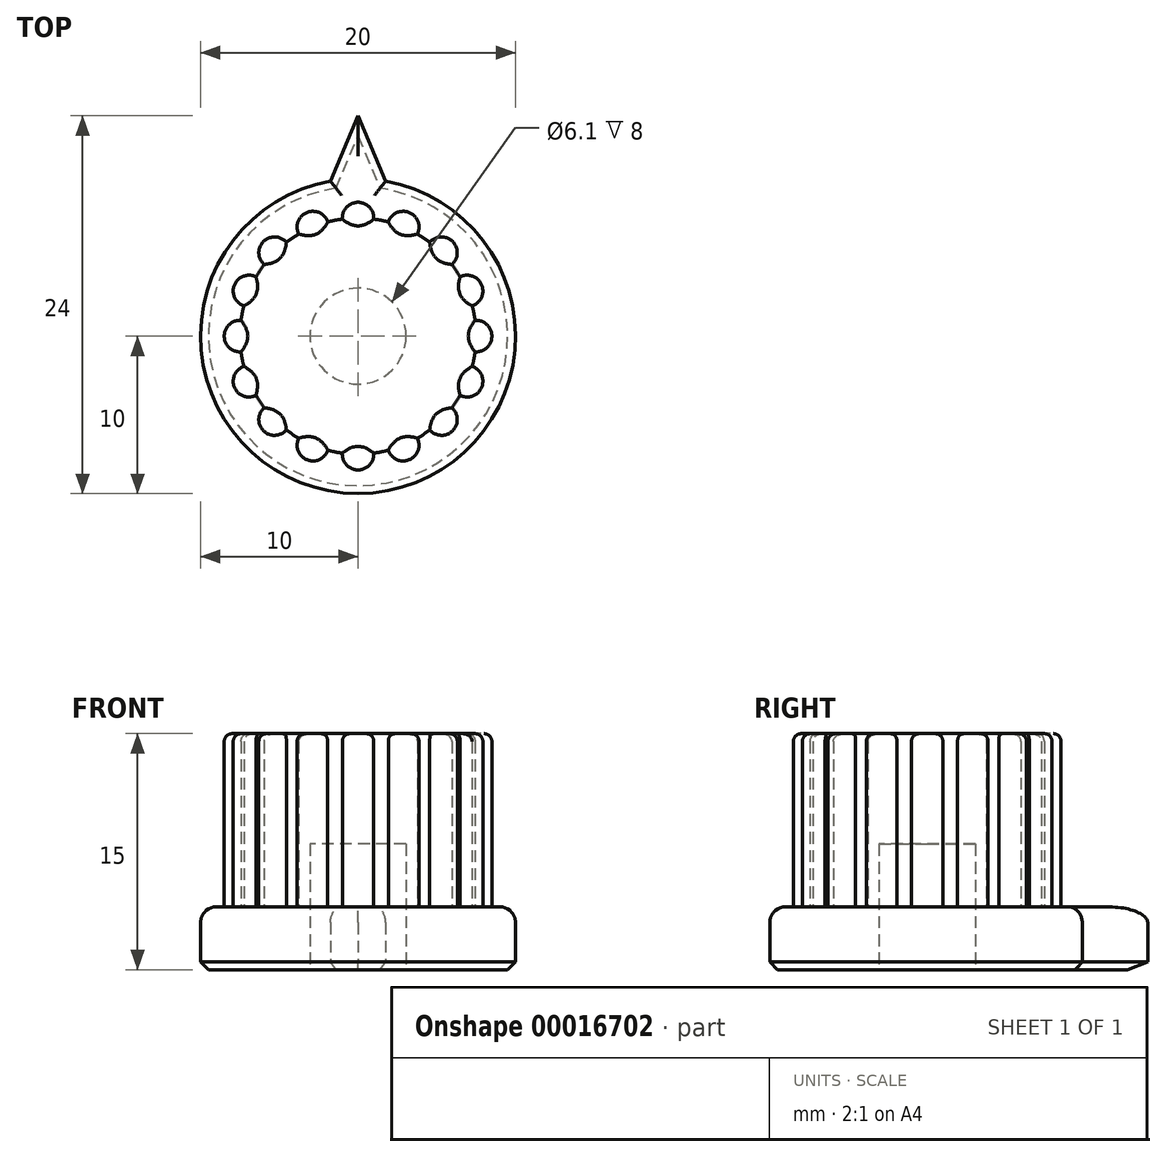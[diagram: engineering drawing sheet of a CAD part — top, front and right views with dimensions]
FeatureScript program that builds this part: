
annotation { "Feature Type Name" : "Feature", "Feature Type Description" : "" }
export const myFeature = defineFeature(function(context is Context, id is Id, definition is map)
    precondition{}
    {
        {
            var Q0;
            Q0=qCreatedBy(makeId("Top.planeOp"),FACE);
            var sketch = newSketch(context, id + "F0", { "sketchPlane" : qUnion([Q0])});
            skCircle(sketch, "E0", {"center": v(0, 0) * mm, "radius": 7.5 * mm});
            skCircle(sketch, "E1", {"center": v(0, 0) * mm, "radius": 10 * mm});
            skCircle(sketch, "E2", {"center": v(0, 0) * mm, "radius": 3.05 * mm});
            skCircle(sketch, "E3", {"center": v(0, 7.5) * mm, "radius": 1 * mm});
            skCircle(sketch, "E4.1.0", {"center": v(2.87, 6.93) * mm, "radius": 1 * mm});
            skCircle(sketch, "E4.2.0", {"center": v(5.3, 5.3) * mm, "radius": 1 * mm});
            skCircle(sketch, "E4.3.0", {"center": v(6.93, 2.87) * mm, "radius": 1 * mm});
            skCircle(sketch, "E4.4.0", {"center": v(7.5, 0) * mm, "radius": 1 * mm});
            skCircle(sketch, "E4.5.0", {"center": v(6.93, -2.87) * mm, "radius": 1 * mm});
            skCircle(sketch, "E4.6.0", {"center": v(5.3, -5.3) * mm, "radius": 1 * mm});
            skCircle(sketch, "E4.7.0", {"center": v(2.87, -6.93) * mm, "radius": 1 * mm});
            skCircle(sketch, "E4.8.0", {"center": v(0, -7.5) * mm, "radius": 1 * mm});
            skCircle(sketch, "E4.9.0", {"center": v(-2.87, -6.93) * mm, "radius": 1 * mm});
            skCircle(sketch, "E4.10.0", {"center": v(-5.3, -5.3) * mm, "radius": 1 * mm});
            skCircle(sketch, "E4.11.0", {"center": v(-6.93, -2.87) * mm, "radius": 1 * mm});
            skCircle(sketch, "E4.12.0", {"center": v(-7.5, 0) * mm, "radius": 1 * mm});
            skCircle(sketch, "E4.13.0", {"center": v(-6.93, 2.87) * mm, "radius": 1 * mm});
            skCircle(sketch, "E4.14.0", {"center": v(-5.3, 5.3) * mm, "radius": 1 * mm});
            skCircle(sketch, "E4.15.0", {"center": v(-2.87, 6.93) * mm, "radius": 1 * mm});
            skLineSegment(sketch, "E4.anchor1", {"start": v(0, 0) * mm, "end": v(0, 7.5) * mm, "construction": true});
            skLineSegment(sketch, "E4.anchor2", {"start": v(0, 0) * mm, "end": v(-2.87, 6.93) * mm, "construction": true});
            skLineSegment(sketch, "E5", {"start": v(0, 10) * mm, "end": v(0, 14) * mm});
            skLineSegment(sketch, "E6", {"start": v(-1.75, 9.85) * mm, "end": v(0, 14) * mm});
            skLineSegment(sketch, "E7.MirrorCS", {"start": v(1.75, 9.85) * mm, "end": v(0, 14) * mm});
            skSolve(sketch);
        }
        {
            var Q0;
            Q0=makeQuery(id+"F0.imprint","IMPRINT",FACE,{"disambiguationData":[TD([[makeQuery(id+"F0.imprint","IMPRINT",EDGE,{"derivedFrom":sQuery(id+"F0.wireOp",EDGE,"E2")}),-1.0]])]});
            var Q1;
            {var subQ0=sQuery(id+"F0.wireOp",EDGE,"E4.12.0");var subQ1=sQuery(id+"F0.wireOp",EDGE,"E0");var subQ3=makeQuery(id+"F0.imprint","INTERSECT",VERTEX,{"disambiguationData":[OD(0.0)],"derivedFrom":[subQ1,subQ0]});Q1=makeQuery(id+"F0.imprint","IMPRINT",FACE,{"disambiguationData":[TD([[makeQuery(id+"F0.imprint","IMPRINT",EDGE,{"disambiguationData":[TD([[subQ3,-1.0]])],"derivedFrom":subQ1}),-1.0]])]});}
            var Q2;
            {var subQ0=sQuery(id+"F0.wireOp",EDGE,"E4.13.0");var subQ1=sQuery(id+"F0.wireOp",EDGE,"E0");var subQ3=makeQuery(id+"F0.imprint","INTERSECT",VERTEX,{"disambiguationData":[OD(0.0)],"derivedFrom":[subQ1,subQ0]});Q2=makeQuery(id+"F0.imprint","IMPRINT",FACE,{"disambiguationData":[TD([[makeQuery(id+"F0.imprint","IMPRINT",EDGE,{"disambiguationData":[TD([[subQ3,-1.0]])],"derivedFrom":subQ1}),-1.0]])]});}
            var Q3;
            {var subQ0=sQuery(id+"F0.wireOp",EDGE,"E4.5.0");var subQ1=sQuery(id+"F0.wireOp",EDGE,"E0");var subQ3=makeQuery(id+"F0.imprint","INTERSECT",VERTEX,{"disambiguationData":[OD(0.0)],"derivedFrom":[subQ1,subQ0]});Q3=makeQuery(id+"F0.imprint","IMPRINT",FACE,{"disambiguationData":[TD([[makeQuery(id+"F0.imprint","IMPRINT",EDGE,{"disambiguationData":[TD([[subQ3,-1.0]])],"derivedFrom":subQ1}),1.0]])]});}
            var Q4;
            {var subQ0=sQuery(id+"F0.wireOp",EDGE,"E4.4.0");var subQ1=sQuery(id+"F0.wireOp",EDGE,"E0");var subQ3=makeQuery(id+"F0.imprint","INTERSECT",VERTEX,{"disambiguationData":[OD(0.0)],"derivedFrom":[subQ1,subQ0]});Q4=makeQuery(id+"F0.imprint","IMPRINT",FACE,{"disambiguationData":[TD([[makeQuery(id+"F0.imprint","IMPRINT",EDGE,{"disambiguationData":[TD([[subQ3,1.0]])],"derivedFrom":subQ1}),-1.0]])]});}
            var Q5;
            {var subQ0=sQuery(id+"F0.wireOp",EDGE,"E4.3.0");var subQ1=sQuery(id+"F0.wireOp",EDGE,"E0");var subQ3=makeQuery(id+"F0.imprint","INTERSECT",VERTEX,{"disambiguationData":[OD(0.0)],"derivedFrom":[subQ1,subQ0]});Q5=makeQuery(id+"F0.imprint","IMPRINT",FACE,{"disambiguationData":[TD([[makeQuery(id+"F0.imprint","IMPRINT",EDGE,{"disambiguationData":[TD([[subQ3,-1.0]])],"derivedFrom":subQ1}),1.0]])]});}
            var Q6;
            {var subQ0=sQuery(id+"F0.wireOp",EDGE,"E4.3.0");var subQ1=sQuery(id+"F0.wireOp",EDGE,"E0");var subQ3=makeQuery(id+"F0.imprint","INTERSECT",VERTEX,{"disambiguationData":[OD(0.0)],"derivedFrom":[subQ1,subQ0]});Q6=makeQuery(id+"F0.imprint","IMPRINT",FACE,{"disambiguationData":[TD([[makeQuery(id+"F0.imprint","IMPRINT",EDGE,{"disambiguationData":[TD([[subQ3,-1.0]])],"derivedFrom":subQ1}),-1.0]])]});}
            var Q7;
            {var subQ0=sQuery(id+"F0.wireOp",EDGE,"E4.2.0");var subQ1=sQuery(id+"F0.wireOp",EDGE,"E0");var subQ3=makeQuery(id+"F0.imprint","INTERSECT",VERTEX,{"disambiguationData":[OD(0.0)],"derivedFrom":[subQ1,subQ0]});Q7=makeQuery(id+"F0.imprint","IMPRINT",FACE,{"disambiguationData":[TD([[makeQuery(id+"F0.imprint","IMPRINT",EDGE,{"disambiguationData":[TD([[subQ3,-1.0]])],"derivedFrom":subQ1}),1.0]])]});}
            var Q8;
            {var subQ0=sQuery(id+"F0.wireOp",EDGE,"E4.2.0");var subQ1=sQuery(id+"F0.wireOp",EDGE,"E0");var subQ3=makeQuery(id+"F0.imprint","INTERSECT",VERTEX,{"disambiguationData":[OD(0.0)],"derivedFrom":[subQ1,subQ0]});Q8=makeQuery(id+"F0.imprint","IMPRINT",FACE,{"disambiguationData":[TD([[makeQuery(id+"F0.imprint","IMPRINT",EDGE,{"disambiguationData":[TD([[subQ3,-1.0]])],"derivedFrom":subQ1}),-1.0]])]});}
            var Q9;
            {var subQ0=sQuery(id+"F0.wireOp",EDGE,"E4.1.0");var subQ1=sQuery(id+"F0.wireOp",EDGE,"E0");var subQ3=makeQuery(id+"F0.imprint","INTERSECT",VERTEX,{"disambiguationData":[OD(0.0)],"derivedFrom":[subQ1,subQ0]});Q9=makeQuery(id+"F0.imprint","IMPRINT",FACE,{"disambiguationData":[TD([[makeQuery(id+"F0.imprint","IMPRINT",EDGE,{"disambiguationData":[TD([[subQ3,-1.0]])],"derivedFrom":subQ1}),1.0]])]});}
            var Q10;
            {var subQ0=sQuery(id+"F0.wireOp",EDGE,"E4.1.0");var subQ1=sQuery(id+"F0.wireOp",EDGE,"E0");var subQ3=makeQuery(id+"F0.imprint","INTERSECT",VERTEX,{"disambiguationData":[OD(0.0)],"derivedFrom":[subQ1,subQ0]});Q10=makeQuery(id+"F0.imprint","IMPRINT",FACE,{"disambiguationData":[TD([[makeQuery(id+"F0.imprint","IMPRINT",EDGE,{"disambiguationData":[TD([[subQ3,-1.0]])],"derivedFrom":subQ1}),-1.0]])]});}
            var Q11;
            {var subQ0=sQuery(id+"F0.wireOp",EDGE,"E3");var subQ1=sQuery(id+"F0.wireOp",EDGE,"E0");var subQ3=makeQuery(id+"F0.imprint","INTERSECT",VERTEX,{"disambiguationData":[OD(0.0)],"derivedFrom":[subQ1,subQ0]});Q11=makeQuery(id+"F0.imprint","IMPRINT",FACE,{"disambiguationData":[TD([[makeQuery(id+"F0.imprint","IMPRINT",EDGE,{"disambiguationData":[TD([[subQ3,-1.0]])],"derivedFrom":subQ1}),1.0]])]});}
            var Q12;
            {var subQ0=sQuery(id+"F0.wireOp",EDGE,"E3");var subQ1=sQuery(id+"F0.wireOp",EDGE,"E0");var subQ3=makeQuery(id+"F0.imprint","INTERSECT",VERTEX,{"disambiguationData":[OD(0.0)],"derivedFrom":[subQ1,subQ0]});Q12=makeQuery(id+"F0.imprint","IMPRINT",FACE,{"disambiguationData":[TD([[makeQuery(id+"F0.imprint","IMPRINT",EDGE,{"disambiguationData":[TD([[subQ3,-1.0]])],"derivedFrom":subQ1}),-1.0]])]});}
            var Q13;
            {var subQ0=sQuery(id+"F0.wireOp",EDGE,"E4.15.0");var subQ1=sQuery(id+"F0.wireOp",EDGE,"E0");var subQ3=makeQuery(id+"F0.imprint","INTERSECT",VERTEX,{"disambiguationData":[OD(0.0)],"derivedFrom":[subQ1,subQ0]});Q13=makeQuery(id+"F0.imprint","IMPRINT",FACE,{"disambiguationData":[TD([[makeQuery(id+"F0.imprint","IMPRINT",EDGE,{"disambiguationData":[TD([[subQ3,-1.0]])],"derivedFrom":subQ1}),1.0]])]});}
            var Q14;
            {var subQ0=sQuery(id+"F0.wireOp",EDGE,"E4.15.0");var subQ1=sQuery(id+"F0.wireOp",EDGE,"E0");var subQ3=makeQuery(id+"F0.imprint","INTERSECT",VERTEX,{"disambiguationData":[OD(0.0)],"derivedFrom":[subQ1,subQ0]});Q14=makeQuery(id+"F0.imprint","IMPRINT",FACE,{"disambiguationData":[TD([[makeQuery(id+"F0.imprint","IMPRINT",EDGE,{"disambiguationData":[TD([[subQ3,-1.0]])],"derivedFrom":subQ1}),-1.0]])]});}
            var Q15;
            {var subQ0=sQuery(id+"F0.wireOp",EDGE,"E4.14.0");var subQ1=sQuery(id+"F0.wireOp",EDGE,"E0");var subQ3=makeQuery(id+"F0.imprint","INTERSECT",VERTEX,{"disambiguationData":[OD(0.0)],"derivedFrom":[subQ1,subQ0]});Q15=makeQuery(id+"F0.imprint","IMPRINT",FACE,{"disambiguationData":[TD([[makeQuery(id+"F0.imprint","IMPRINT",EDGE,{"disambiguationData":[TD([[subQ3,-1.0]])],"derivedFrom":subQ1}),1.0]])]});}
            var Q16;
            {var subQ0=sQuery(id+"F0.wireOp",EDGE,"E4.14.0");var subQ1=sQuery(id+"F0.wireOp",EDGE,"E0");var subQ3=makeQuery(id+"F0.imprint","INTERSECT",VERTEX,{"disambiguationData":[OD(0.0)],"derivedFrom":[subQ1,subQ0]});Q16=makeQuery(id+"F0.imprint","IMPRINT",FACE,{"disambiguationData":[TD([[makeQuery(id+"F0.imprint","IMPRINT",EDGE,{"disambiguationData":[TD([[subQ3,-1.0]])],"derivedFrom":subQ1}),-1.0]])]});}
            var Q17;
            {var subQ0=sQuery(id+"F0.wireOp",EDGE,"E4.5.0");var subQ1=sQuery(id+"F0.wireOp",EDGE,"E0");var subQ3=makeQuery(id+"F0.imprint","INTERSECT",VERTEX,{"disambiguationData":[OD(0.0)],"derivedFrom":[subQ1,subQ0]});Q17=makeQuery(id+"F0.imprint","IMPRINT",FACE,{"disambiguationData":[TD([[makeQuery(id+"F0.imprint","IMPRINT",EDGE,{"disambiguationData":[TD([[subQ3,-1.0]])],"derivedFrom":subQ1}),-1.0]])]});}
            var Q18;
            {var subQ0=sQuery(id+"F0.wireOp",EDGE,"E4.4.0");var subQ1=sQuery(id+"F0.wireOp",EDGE,"E0");var subQ3=makeQuery(id+"F0.imprint","INTERSECT",VERTEX,{"disambiguationData":[OD(0.0)],"derivedFrom":[subQ1,subQ0]});Q18=makeQuery(id+"F0.imprint","IMPRINT",FACE,{"disambiguationData":[TD([[makeQuery(id+"F0.imprint","IMPRINT",EDGE,{"disambiguationData":[TD([[subQ3,1.0]])],"derivedFrom":subQ1}),1.0]])]});}
            var Q19;
            {var subQ0=sQuery(id+"F0.wireOp",EDGE,"E4.7.0");var subQ1=sQuery(id+"F0.wireOp",EDGE,"E0");var subQ3=makeQuery(id+"F0.imprint","INTERSECT",VERTEX,{"disambiguationData":[OD(0.0)],"derivedFrom":[subQ1,subQ0]});Q19=makeQuery(id+"F0.imprint","IMPRINT",FACE,{"disambiguationData":[TD([[makeQuery(id+"F0.imprint","IMPRINT",EDGE,{"disambiguationData":[TD([[subQ3,-1.0]])],"derivedFrom":subQ1}),-1.0]])]});}
            var Q20;
            {var subQ0=sQuery(id+"F0.wireOp",EDGE,"E4.12.0");var subQ1=sQuery(id+"F0.wireOp",EDGE,"E0");var subQ3=makeQuery(id+"F0.imprint","INTERSECT",VERTEX,{"disambiguationData":[OD(0.0)],"derivedFrom":[subQ1,subQ0]});Q20=makeQuery(id+"F0.imprint","IMPRINT",FACE,{"disambiguationData":[TD([[makeQuery(id+"F0.imprint","IMPRINT",EDGE,{"disambiguationData":[TD([[subQ3,-1.0]])],"derivedFrom":subQ1}),1.0]])]});}
            var Q21;
            {var subQ0=sQuery(id+"F0.wireOp",EDGE,"E4.10.0");var subQ1=sQuery(id+"F0.wireOp",EDGE,"E0");var subQ3=makeQuery(id+"F0.imprint","INTERSECT",VERTEX,{"disambiguationData":[OD(0.0)],"derivedFrom":[subQ1,subQ0]});Q21=makeQuery(id+"F0.imprint","IMPRINT",FACE,{"disambiguationData":[TD([[makeQuery(id+"F0.imprint","IMPRINT",EDGE,{"disambiguationData":[TD([[subQ3,-1.0]])],"derivedFrom":subQ1}),-1.0]])]});}
            var Q22;
            {var subQ0=sQuery(id+"F0.wireOp",EDGE,"E4.10.0");var subQ1=sQuery(id+"F0.wireOp",EDGE,"E0");var subQ3=makeQuery(id+"F0.imprint","INTERSECT",VERTEX,{"disambiguationData":[OD(0.0)],"derivedFrom":[subQ1,subQ0]});Q22=makeQuery(id+"F0.imprint","IMPRINT",FACE,{"disambiguationData":[TD([[makeQuery(id+"F0.imprint","IMPRINT",EDGE,{"disambiguationData":[TD([[subQ3,-1.0]])],"derivedFrom":subQ1}),1.0]])]});}
            var Q23;
            {var subQ0=sQuery(id+"F0.wireOp",EDGE,"E4.9.0");var subQ1=sQuery(id+"F0.wireOp",EDGE,"E0");var subQ3=makeQuery(id+"F0.imprint","INTERSECT",VERTEX,{"disambiguationData":[OD(0.0)],"derivedFrom":[subQ1,subQ0]});Q23=makeQuery(id+"F0.imprint","IMPRINT",FACE,{"disambiguationData":[TD([[makeQuery(id+"F0.imprint","IMPRINT",EDGE,{"disambiguationData":[TD([[subQ3,-1.0]])],"derivedFrom":subQ1}),-1.0]])]});}
            var Q24;
            {var subQ0=sQuery(id+"F0.wireOp",EDGE,"E4.13.0");var subQ1=sQuery(id+"F0.wireOp",EDGE,"E0");var subQ3=makeQuery(id+"F0.imprint","INTERSECT",VERTEX,{"disambiguationData":[OD(0.0)],"derivedFrom":[subQ1,subQ0]});Q24=makeQuery(id+"F0.imprint","IMPRINT",FACE,{"disambiguationData":[TD([[makeQuery(id+"F0.imprint","IMPRINT",EDGE,{"disambiguationData":[TD([[subQ3,-1.0]])],"derivedFrom":subQ1}),1.0]])]});}
            var Q25;
            {var subQ0=sQuery(id+"F0.wireOp",EDGE,"E4.6.0");var subQ1=sQuery(id+"F0.wireOp",EDGE,"E0");var subQ3=makeQuery(id+"F0.imprint","INTERSECT",VERTEX,{"disambiguationData":[OD(0.0)],"derivedFrom":[subQ1,subQ0]});Q25=makeQuery(id+"F0.imprint","IMPRINT",FACE,{"disambiguationData":[TD([[makeQuery(id+"F0.imprint","IMPRINT",EDGE,{"disambiguationData":[TD([[subQ3,-1.0]])],"derivedFrom":subQ1}),1.0]])]});}
            var Q26;
            {var subQ0=sQuery(id+"F0.wireOp",EDGE,"E4.8.0");var subQ1=sQuery(id+"F0.wireOp",EDGE,"E0");var subQ3=makeQuery(id+"F0.imprint","INTERSECT",VERTEX,{"disambiguationData":[OD(0.0)],"derivedFrom":[subQ1,subQ0]});Q26=makeQuery(id+"F0.imprint","IMPRINT",FACE,{"disambiguationData":[TD([[makeQuery(id+"F0.imprint","IMPRINT",EDGE,{"disambiguationData":[TD([[subQ3,-1.0]])],"derivedFrom":subQ1}),1.0]])]});}
            var Q27;
            {var subQ0=sQuery(id+"F0.wireOp",EDGE,"E4.9.0");var subQ1=sQuery(id+"F0.wireOp",EDGE,"E0");var subQ3=makeQuery(id+"F0.imprint","INTERSECT",VERTEX,{"disambiguationData":[OD(0.0)],"derivedFrom":[subQ1,subQ0]});Q27=makeQuery(id+"F0.imprint","IMPRINT",FACE,{"disambiguationData":[TD([[makeQuery(id+"F0.imprint","IMPRINT",EDGE,{"disambiguationData":[TD([[subQ3,-1.0]])],"derivedFrom":subQ1}),1.0]])]});}
            var Q28;
            {var subQ0=sQuery(id+"F0.wireOp",EDGE,"E4.11.0");var subQ1=sQuery(id+"F0.wireOp",EDGE,"E0");var subQ3=makeQuery(id+"F0.imprint","INTERSECT",VERTEX,{"disambiguationData":[OD(0.0)],"derivedFrom":[subQ1,subQ0]});Q28=makeQuery(id+"F0.imprint","IMPRINT",FACE,{"disambiguationData":[TD([[makeQuery(id+"F0.imprint","IMPRINT",EDGE,{"disambiguationData":[TD([[subQ3,-1.0]])],"derivedFrom":subQ1}),1.0]])]});}
            var Q29;
            {var subQ0=sQuery(id+"F0.wireOp",EDGE,"E4.6.0");var subQ1=sQuery(id+"F0.wireOp",EDGE,"E0");var subQ3=makeQuery(id+"F0.imprint","INTERSECT",VERTEX,{"disambiguationData":[OD(0.0)],"derivedFrom":[subQ1,subQ0]});Q29=makeQuery(id+"F0.imprint","IMPRINT",FACE,{"disambiguationData":[TD([[makeQuery(id+"F0.imprint","IMPRINT",EDGE,{"disambiguationData":[TD([[subQ3,-1.0]])],"derivedFrom":subQ1}),-1.0]])]});}
            var Q30;
            {var subQ0=sQuery(id+"F0.wireOp",EDGE,"E4.8.0");var subQ1=sQuery(id+"F0.wireOp",EDGE,"E0");var subQ3=makeQuery(id+"F0.imprint","INTERSECT",VERTEX,{"disambiguationData":[OD(0.0)],"derivedFrom":[subQ1,subQ0]});Q30=makeQuery(id+"F0.imprint","IMPRINT",FACE,{"disambiguationData":[TD([[makeQuery(id+"F0.imprint","IMPRINT",EDGE,{"disambiguationData":[TD([[subQ3,-1.0]])],"derivedFrom":subQ1}),-1.0]])]});}
            var Q31;
            {var subQ0=sQuery(id+"F0.wireOp",EDGE,"E4.11.0");var subQ1=sQuery(id+"F0.wireOp",EDGE,"E0");var subQ3=makeQuery(id+"F0.imprint","INTERSECT",VERTEX,{"disambiguationData":[OD(0.0)],"derivedFrom":[subQ1,subQ0]});Q31=makeQuery(id+"F0.imprint","IMPRINT",FACE,{"disambiguationData":[TD([[makeQuery(id+"F0.imprint","IMPRINT",EDGE,{"disambiguationData":[TD([[subQ3,-1.0]])],"derivedFrom":subQ1}),-1.0]])]});}
            var Q32;
            {var subQ0=sQuery(id+"F0.wireOp",EDGE,"E4.7.0");var subQ1=sQuery(id+"F0.wireOp",EDGE,"E0");var subQ3=makeQuery(id+"F0.imprint","INTERSECT",VERTEX,{"disambiguationData":[OD(0.0)],"derivedFrom":[subQ1,subQ0]});Q32=makeQuery(id+"F0.imprint","IMPRINT",FACE,{"disambiguationData":[TD([[makeQuery(id+"F0.imprint","IMPRINT",EDGE,{"disambiguationData":[TD([[subQ3,-1.0]])],"derivedFrom":subQ1}),1.0]])]});}
            var Q33;
            Q33=makeQuery(id+"F0.imprint","IMPRINT",FACE,{"disambiguationData":[TD([[makeQuery(id+"F0.imprint","IMPRINT",EDGE,{"derivedFrom":sQuery(id+"F0.wireOp",EDGE,"E2")}),1.0]])]});
            extrude(context, id + "F1", {"entities" : qUnion([Q0, Q1, Q2, Q3, Q4, Q5, Q6, Q7, Q8, Q9, Q10, Q11, Q12, Q13, Q14, Q15, Q16, Q17, Q18, Q19, Q20, Q21, Q22, Q23, Q24, Q25, Q26, Q27, Q28, Q29, Q30, Q31, Q32, Q33]), "depth" : 15 * mm});
        }
        {
            var Q0;
            Q0=makeQuery(id+"F0.imprint","IMPRINT",FACE,{"disambiguationData":[TD([[makeQuery(id+"F0.imprint","IMPRINT",EDGE,{"derivedFrom":sQuery(id+"F0.wireOp",EDGE,"E1")}),1.0]])]});
            var Q1;
            {var subQ1=sQuery(id+"F0.wireOp",EDGE,"E5");Q1=makeQuery(id+"F0.imprint","IMPRINT",FACE,{"disambiguationData":[TD([[makeQuery(id+"F0.imprint","IMPRINT",EDGE,{"derivedFrom":subQ1}),-1.0]])]});}
            var Q2;
            {var subQ1=sQuery(id+"F0.wireOp",EDGE,"E5");Q2=makeQuery(id+"F0.imprint","IMPRINT",FACE,{"disambiguationData":[TD([[makeQuery(id+"F0.imprint","IMPRINT",EDGE,{"derivedFrom":subQ1}),1.0]])]});}
            extrude(context, id + "F2", {"entities" : qUnion([Q0, Q1, Q2]), "operationType" : NewBodyOperationType.ADD, "depth" : 4 * mm});
        }
        {
            var Q0;
            Q0=makeQuery(id+"F0.imprint","IMPRINT",FACE,{"disambiguationData":[TD([[makeQuery(id+"F0.imprint","IMPRINT",EDGE,{"derivedFrom":sQuery(id+"F0.wireOp",EDGE,"E2")}),1.0]])]});
            extrude(context, id + "F3", {"entities" : qUnion([Q0]), "operationType" : NewBodyOperationType.REMOVE, "depth" : 8 * mm});
        }
        {
            var Q0;
            Q0=makeQuery(id+"F2.opExtrude","CAP_EDGE",EDGE,{"disambiguationData":[OSD([sQuery(id+"F0.wireOp",EDGE,"E1")])],"isStart":false});
            var Q1;
            Q1=makeQuery(id+"F2.opExtrude","CAP_EDGE",EDGE,{"disambiguationData":[OSD([sQuery(id+"F0.wireOp",EDGE,"be9af46f-8be3-4fce-9193-26453e98453a")])],"isStart":false});
            var Q2;
            Q2=makeQuery(id+"F2.opExtrude","CAP_EDGE",EDGE,{"disambiguationData":[OSD([sQuery(id+"F0.wireOp",EDGE,"E6")])],"isStart":false});
            var Q3;
            Q3=makeQuery(id+"F2.opExtrude","CAP_EDGE",EDGE,{"disambiguationData":[OSD([sQuery(id+"F0.wireOp",EDGE,"E7.MirrorCS")])],"isStart":false});
            fillet(context, id + "F4", {"entities" : qUnion([Q0, Q1, Q2, Q3]), "radius" : 1 * mm, "tangentPropagation" : true, "allowEdgeOverflow" : false});
        }
        {
            var Q0;
            Q0=makeQuery(id+"F2.opExtrude","CAP_EDGE",EDGE,{"disambiguationData":[OSD([sQuery(id+"F0.wireOp",EDGE,"E1")])],"isStart":true});
            var Q1;
            Q1=makeQuery(id+"F2.opExtrude","CAP_EDGE",EDGE,{"disambiguationData":[OSD([sQuery(id+"F0.wireOp",EDGE,"E6")])],"isStart":true});
            var Q2;
            Q2=makeQuery(id+"F2.opExtrude","CAP_EDGE",EDGE,{"disambiguationData":[OSD([sQuery(id+"F0.wireOp",EDGE,"be9af46f-8be3-4fce-9193-26453e98453a")])],"isStart":true});
            var Q3;
            Q3=makeQuery(id+"F2.opExtrude","CAP_EDGE",EDGE,{"disambiguationData":[OSD([sQuery(id+"F0.wireOp",EDGE,"E7.MirrorCS")])],"isStart":true});
            chamfer(context, id + "F5", {"entities" : qUnion([Q0, Q1, Q2, Q3]), "width" : 0.5 * mm, "tangentPropagation" : true});
        }
        {
            var Q0;
            Q0=makeQuery(id+"F1.opExtrude","CAP_EDGE",EDGE,{"disambiguationData":[OSD([sQuery(id+"F0.wireOp",EDGE,"E4.12.0")])],"isStart":false});
            var Q1;
            Q1=makeQuery(id+"F1.opExtrude","CAP_EDGE",EDGE,{"disambiguationData":[OSD([sQuery(id+"F0.wireOp",EDGE,"E4.5.0")])],"isStart":false});
            var Q2;
            Q2=makeQuery(id+"F1.opExtrude","CAP_EDGE",EDGE,{"disambiguationData":[OSD([sQuery(id+"F0.wireOp",EDGE,"E4.10.0")])],"isStart":false});
            var Q3;
            {var subQ0=sQuery(id+"F0.wireOp",EDGE,"E0");Q3=makeQuery(id+"F1.opExtrude","CAP_EDGE",EDGE,{"disambiguationData":[OSD([subQ0]),TDD([makeQuery(id+"F0.imprint","IMPRINT",EDGE,{"disambiguationData":[TD([[makeQuery(id+"F0.imprint","INTERSECT",VERTEX,{"disambiguationData":[OD(1.0)],"derivedFrom":[subQ0,sQuery(id+"F0.wireOp",EDGE,"E4.2.0")]}),-1.0]])],"derivedFrom":subQ0})])],"isStart":false});}
            var Q4;
            Q4=makeQuery(id+"F1.opExtrude","CAP_EDGE",EDGE,{"disambiguationData":[OSD([sQuery(id+"F0.wireOp",EDGE,"E4.6.0")])],"isStart":false});
            var Q5;
            Q5=makeQuery(id+"F1.opExtrude","CAP_EDGE",EDGE,{"disambiguationData":[OSD([sQuery(id+"F0.wireOp",EDGE,"E4.11.0")])],"isStart":false});
            var Q6;
            Q6=makeQuery(id+"F1.opExtrude","CAP_EDGE",EDGE,{"disambiguationData":[OSD([sQuery(id+"F0.wireOp",EDGE,"E4.13.0")])],"isStart":false});
            var Q7;
            Q7=makeQuery(id+"F1.opExtrude","CAP_EDGE",EDGE,{"disambiguationData":[OSD([sQuery(id+"F0.wireOp",EDGE,"E4.4.0")])],"isStart":false});
            var Q8;
            {var subQ0=sQuery(id+"F0.wireOp",EDGE,"E0");Q8=makeQuery(id+"F1.opExtrude","CAP_EDGE",EDGE,{"disambiguationData":[OSD([subQ0]),TDD([makeQuery(id+"F0.imprint","IMPRINT",EDGE,{"disambiguationData":[TD([[makeQuery(id+"F0.imprint","INTERSECT",VERTEX,{"disambiguationData":[OD(1.0)],"derivedFrom":[subQ0,sQuery(id+"F0.wireOp",EDGE,"E4.8.0")]}),-1.0]])],"derivedFrom":subQ0})])],"isStart":false});}
            var Q9;
            {var subQ0=sQuery(id+"F0.wireOp",EDGE,"E0");Q9=makeQuery(id+"F1.opExtrude","CAP_EDGE",EDGE,{"disambiguationData":[OSD([subQ0]),TDD([makeQuery(id+"F0.imprint","IMPRINT",EDGE,{"disambiguationData":[TD([[makeQuery(id+"F0.imprint","INTERSECT",VERTEX,{"disambiguationData":[OD(1.0)],"derivedFrom":[subQ0,sQuery(id+"F0.wireOp",EDGE,"E4.15.0")]}),-1.0]])],"derivedFrom":subQ0})])],"isStart":false});}
            var Q10;
            Q10=makeQuery(id+"F1.opExtrude","CAP_EDGE",EDGE,{"disambiguationData":[OSD([sQuery(id+"F0.wireOp",EDGE,"E4.15.0")])],"isStart":false});
            var Q11;
            {var subQ0=sQuery(id+"F0.wireOp",EDGE,"E0");Q11=makeQuery(id+"F1.opExtrude","CAP_EDGE",EDGE,{"disambiguationData":[OSD([subQ0]),TDD([makeQuery(id+"F0.imprint","IMPRINT",EDGE,{"disambiguationData":[TD([[makeQuery(id+"F0.imprint","INTERSECT",VERTEX,{"disambiguationData":[OD(1.0)],"derivedFrom":[subQ0,sQuery(id+"F0.wireOp",EDGE,"E4.13.0")]}),-1.0]])],"derivedFrom":subQ0})])],"isStart":false});}
            var Q12;
            Q12=makeQuery(id+"F1.opExtrude","CAP_EDGE",EDGE,{"disambiguationData":[OSD([sQuery(id+"F0.wireOp",EDGE,"E4.2.0")])],"isStart":false});
            var Q13;
            {var subQ0=sQuery(id+"F0.wireOp",EDGE,"E0");Q13=makeQuery(id+"F1.opExtrude","CAP_EDGE",EDGE,{"disambiguationData":[OSD([subQ0]),TDD([makeQuery(id+"F0.imprint","IMPRINT",EDGE,{"disambiguationData":[TD([[makeQuery(id+"F0.imprint","INTERSECT",VERTEX,{"disambiguationData":[OD(1.0)],"derivedFrom":[subQ0,sQuery(id+"F0.wireOp",EDGE,"E4.9.0")]}),-1.0]])],"derivedFrom":subQ0})])],"isStart":false});}
            var Q14;
            {var subQ0=sQuery(id+"F0.wireOp",EDGE,"E0");Q14=makeQuery(id+"F1.opExtrude","CAP_EDGE",EDGE,{"disambiguationData":[OSD([subQ0]),TDD([makeQuery(id+"F0.imprint","IMPRINT",EDGE,{"disambiguationData":[TD([[makeQuery(id+"F0.imprint","INTERSECT",VERTEX,{"disambiguationData":[OD(1.0)],"derivedFrom":[subQ0,sQuery(id+"F0.wireOp",EDGE,"E4.10.0")]}),-1.0]])],"derivedFrom":subQ0})])],"isStart":false});}
            var Q15;
            Q15=makeQuery(id+"F1.opExtrude","CAP_EDGE",EDGE,{"disambiguationData":[OSD([sQuery(id+"F0.wireOp",EDGE,"E3")])],"isStart":false});
            var Q16;
            {var subQ0=sQuery(id+"F0.wireOp",EDGE,"E0");Q16=makeQuery(id+"F1.opExtrude","CAP_EDGE",EDGE,{"disambiguationData":[OSD([subQ0]),TDD([makeQuery(id+"F0.imprint","IMPRINT",EDGE,{"disambiguationData":[TD([[makeQuery(id+"F0.imprint","INTERSECT",VERTEX,{"disambiguationData":[OD(1.0)],"derivedFrom":[subQ0,sQuery(id+"F0.wireOp",EDGE,"E4.12.0")]}),-1.0]])],"derivedFrom":subQ0})])],"isStart":false});}
            var Q17;
            Q17=makeQuery(id+"F1.opExtrude","CAP_EDGE",EDGE,{"disambiguationData":[OSD([sQuery(id+"F0.wireOp",EDGE,"E4.8.0")])],"isStart":false});
            var Q18;
            {var subQ0=sQuery(id+"F0.wireOp",EDGE,"E0");Q18=makeQuery(id+"F1.opExtrude","CAP_EDGE",EDGE,{"disambiguationData":[OSD([subQ0]),TDD([makeQuery(id+"F0.imprint","IMPRINT",EDGE,{"disambiguationData":[TD([[makeQuery(id+"F0.imprint","INTERSECT",VERTEX,{"disambiguationData":[OD(1.0)],"derivedFrom":[subQ0,sQuery(id+"F0.wireOp",EDGE,"E4.6.0")]}),-1.0]])],"derivedFrom":subQ0})])],"isStart":false});}
            var Q19;
            Q19=makeQuery(id+"F1.opExtrude","CAP_EDGE",EDGE,{"disambiguationData":[OSD([sQuery(id+"F0.wireOp",EDGE,"E4.14.0")])],"isStart":false});
            var Q20;
            {var subQ0=sQuery(id+"F0.wireOp",EDGE,"E0");Q20=makeQuery(id+"F1.opExtrude","CAP_EDGE",EDGE,{"disambiguationData":[OSD([subQ0]),TDD([makeQuery(id+"F0.imprint","IMPRINT",EDGE,{"disambiguationData":[TD([[makeQuery(id+"F0.imprint","INTERSECT",VERTEX,{"disambiguationData":[OD(1.0)],"derivedFrom":[subQ0,sQuery(id+"F0.wireOp",EDGE,"E4.1.0")]}),-1.0]])],"derivedFrom":subQ0})])],"isStart":false});}
            var Q21;
            Q21=makeQuery(id+"F1.opExtrude","CAP_EDGE",EDGE,{"disambiguationData":[OSD([sQuery(id+"F0.wireOp",EDGE,"E4.3.0")])],"isStart":false});
            var Q22;
            {var subQ0=sQuery(id+"F0.wireOp",EDGE,"E0");Q22=makeQuery(id+"F1.opExtrude","CAP_EDGE",EDGE,{"disambiguationData":[OSD([subQ0]),TDD([makeQuery(id+"F0.imprint","IMPRINT",EDGE,{"disambiguationData":[TD([[makeQuery(id+"F0.imprint","INTERSECT",VERTEX,{"disambiguationData":[OD(1.0)],"derivedFrom":[subQ0,sQuery(id+"F0.wireOp",EDGE,"E4.14.0")]}),-1.0]])],"derivedFrom":subQ0})])],"isStart":false});}
            var Q23;
            {var subQ0=sQuery(id+"F0.wireOp",EDGE,"E0");Q23=makeQuery(id+"F1.opExtrude","CAP_EDGE",EDGE,{"disambiguationData":[OSD([subQ0]),TDD([makeQuery(id+"F0.imprint","IMPRINT",EDGE,{"disambiguationData":[TD([[makeQuery(id+"F0.imprint","INTERSECT",VERTEX,{"disambiguationData":[OD(1.0)],"derivedFrom":[subQ0,sQuery(id+"F0.wireOp",EDGE,"E4.7.0")]}),-1.0]])],"derivedFrom":subQ0})])],"isStart":false});}
            var Q24;
            {var subQ0=sQuery(id+"F0.wireOp",EDGE,"E0");Q24=makeQuery(id+"F1.opExtrude","CAP_EDGE",EDGE,{"disambiguationData":[OSD([subQ0]),TDD([makeQuery(id+"F0.imprint","IMPRINT",EDGE,{"disambiguationData":[TD([[makeQuery(id+"F0.imprint","INTERSECT",VERTEX,{"disambiguationData":[OD(1.0)],"derivedFrom":[subQ0,sQuery(id+"F0.wireOp",EDGE,"E3")]}),-1.0]])],"derivedFrom":subQ0})])],"isStart":false});}
            var Q25;
            {var subQ0=sQuery(id+"F0.wireOp",EDGE,"E0");Q25=makeQuery(id+"F1.opExtrude","CAP_EDGE",EDGE,{"disambiguationData":[OSD([subQ0]),TDD([makeQuery(id+"F0.imprint","IMPRINT",EDGE,{"disambiguationData":[TD([[makeQuery(id+"F0.imprint","INTERSECT",VERTEX,{"disambiguationData":[OD(0.0)],"derivedFrom":[subQ0,sQuery(id+"F0.wireOp",EDGE,"E4.3.0")]}),1.0]])],"derivedFrom":subQ0})])],"isStart":false});}
            var Q26;
            {var subQ0=sQuery(id+"F0.wireOp",EDGE,"E0");Q26=makeQuery(id+"F1.opExtrude","CAP_EDGE",EDGE,{"disambiguationData":[OSD([subQ0]),TDD([makeQuery(id+"F0.imprint","IMPRINT",EDGE,{"disambiguationData":[TD([[makeQuery(id+"F0.imprint","INTERSECT",VERTEX,{"disambiguationData":[OD(1.0)],"derivedFrom":[subQ0,sQuery(id+"F0.wireOp",EDGE,"E4.5.0")]}),-1.0]])],"derivedFrom":subQ0})])],"isStart":false});}
            var Q27;
            Q27=makeQuery(id+"F1.opExtrude","CAP_EDGE",EDGE,{"disambiguationData":[OSD([sQuery(id+"F0.wireOp",EDGE,"E4.7.0")])],"isStart":false});
            var Q28;
            {var subQ0=sQuery(id+"F0.wireOp",EDGE,"E0");Q28=makeQuery(id+"F1.opExtrude","CAP_EDGE",EDGE,{"disambiguationData":[OSD([subQ0]),TDD([makeQuery(id+"F0.imprint","IMPRINT",EDGE,{"disambiguationData":[TD([[makeQuery(id+"F0.imprint","INTERSECT",VERTEX,{"disambiguationData":[OD(1.0)],"derivedFrom":[subQ0,sQuery(id+"F0.wireOp",EDGE,"E4.11.0")]}),-1.0]])],"derivedFrom":subQ0})])],"isStart":false});}
            var Q29;
            {var subQ0=sQuery(id+"F0.wireOp",EDGE,"E0");Q29=makeQuery(id+"F1.opExtrude","CAP_EDGE",EDGE,{"disambiguationData":[OSD([subQ0]),TDD([makeQuery(id+"F0.imprint","IMPRINT",EDGE,{"disambiguationData":[TD([[makeQuery(id+"F0.imprint","INTERSECT",VERTEX,{"disambiguationData":[OD(1.0)],"derivedFrom":[subQ0,sQuery(id+"F0.wireOp",EDGE,"E4.3.0")]}),-1.0]])],"derivedFrom":subQ0})])],"isStart":false});}
            var Q30;
            Q30=makeQuery(id+"F1.opExtrude","CAP_EDGE",EDGE,{"disambiguationData":[OSD([sQuery(id+"F0.wireOp",EDGE,"E4.9.0")])],"isStart":false});
            var Q31;
            Q31=makeQuery(id+"F1.opExtrude","CAP_EDGE",EDGE,{"disambiguationData":[OSD([sQuery(id+"F0.wireOp",EDGE,"E4.1.0")])],"isStart":false});
            fillet(context, id + "F6", {"entities" : qUnion([Q0, Q1, Q2, Q3, Q4, Q5, Q6, Q7, Q8, Q9, Q10, Q11, Q12, Q13, Q14, Q15, Q16, Q17, Q18, Q19, Q20, Q21, Q22, Q23, Q24, Q25, Q26, Q27, Q28, Q29, Q30, Q31]), "radius" : 0.5 * mm, "allowEdgeOverflow" : false});
        }
    });
